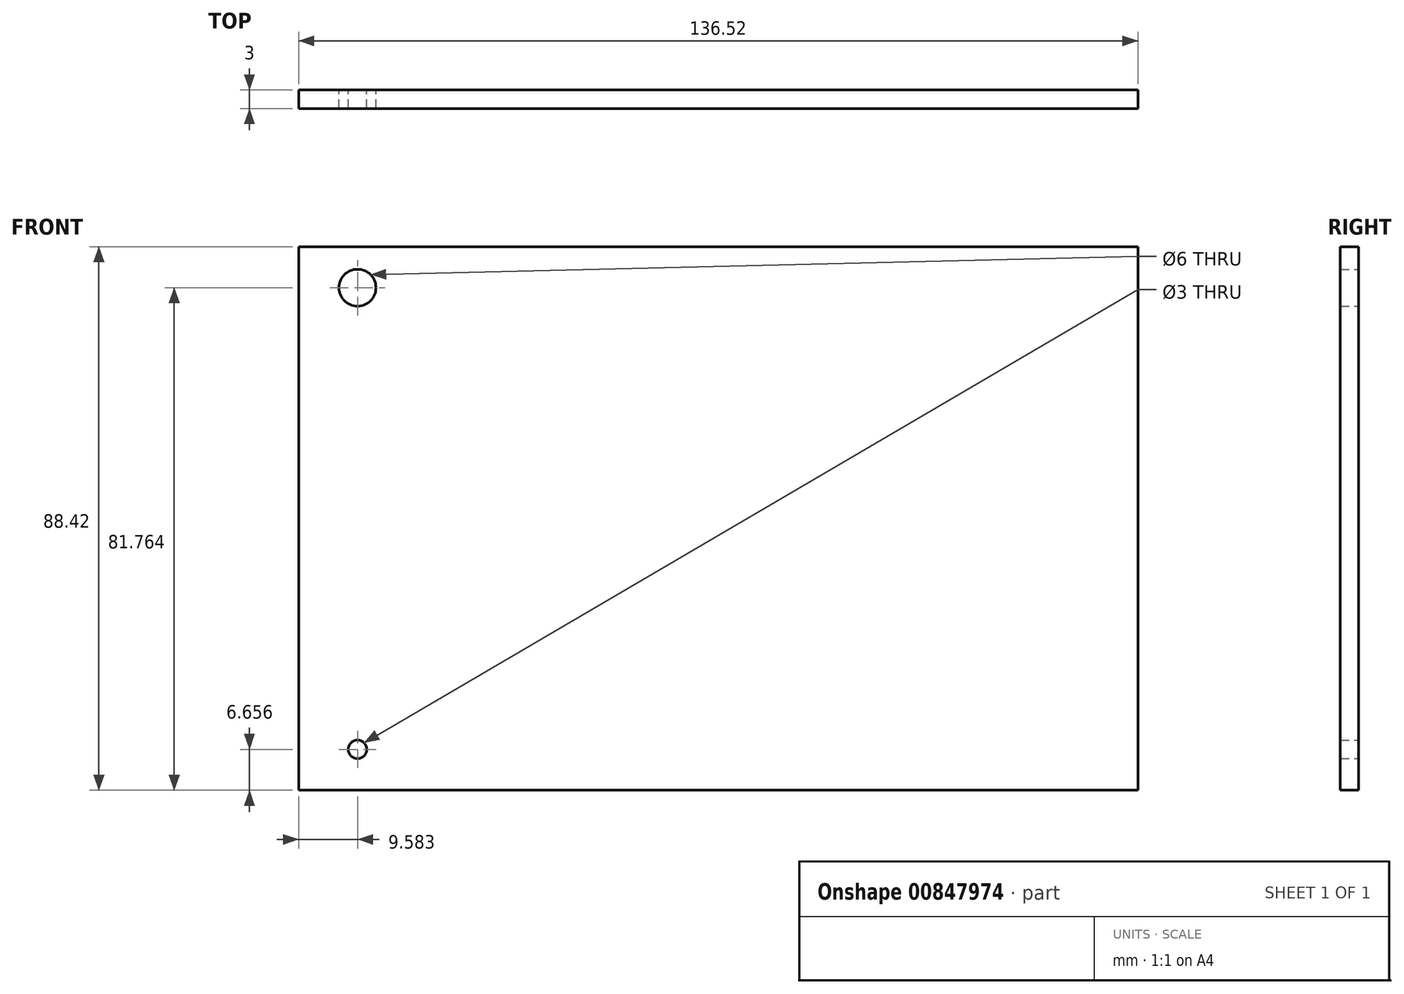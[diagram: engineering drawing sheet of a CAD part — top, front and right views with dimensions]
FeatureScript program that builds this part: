
annotation { "Feature Type Name" : "Feature", "Feature Type Description" : "" }
export const myFeature = defineFeature(function(context is Context, id is Id, definition is map)
    precondition{}
    {
        {
            var Q0;
            Q0=qCreatedBy(makeId("Front.planeOp"),FACE);
            var sketch = newSketch(context, id + "F0", { "sketchPlane" : qUnion([Q0])});
            skLineSegment(sketch, "E0.bottom", {"start": v(68.26, 44.21) * mm, "end": v(-68.26, 44.21) * mm});
            skLineSegment(sketch, "E0.top", {"start": v(68.26, -44.21) * mm, "end": v(-68.26, -44.21) * mm});
            skLineSegment(sketch, "E0.left", {"start": v(68.26, 44.21) * mm, "end": v(68.26, -44.21) * mm});
            skLineSegment(sketch, "E0.right", {"start": v(-68.26, 44.21) * mm, "end": v(-68.26, -44.21) * mm});
            skPoint(sketch, "E0.middle", {"position": v(0, 0) * mm});
            skSolve(sketch);
        }
        {
            var Q0;
            Q0=makeQuery(id+"F0.imprint","IMPRINT",FACE,{"disambiguationData":[TD([[makeQuery(id+"F0.imprint","IMPRINT",EDGE,{"derivedFrom":sQuery(id+"F0.wireOp",EDGE,"E0.bottom")}),1.0]])]});
            extrude(context, id + "F1", {"entities" : qUnion([Q0]), "depth" : 3 * mm, "offsetDistance" : 25.4 * mm});
        }
        {
            var Q0;
            Q0=sQuery(id+"F0.wireOp",VERTEX,"E0.middle");
            var Q1;
            Q1=makeQuery(id+"F1.opExtrude","SWEPT_BODY",BODY,{"disambiguationData":[OSD([sQuery(id+"F0.wireOp",EDGE,"E0.bottom"),sQuery(id+"F0.wireOp",EDGE,"E0.top"),sQuery(id+"F0.wireOp",EDGE,"E0.left"),sQuery(id+"F0.wireOp",EDGE,"E0.right")])]});
            hole(context, id + "F2", {"style" : HoleStyle.SIMPLE, "endStyle" : HoleEndStyle.THROUGH, "oppositeDirection" : true, "holeDiameter" : 30 * mm, "majorDiameter" : 6.35 * mm, "isTappedThrough" : true, "tappedDepth" : 12.7 * mm, "tapClearance" : 3, "locations" : qUnion([Q0]), "scope" : qUnion([Q1])});
        }
        {
            var Q0;
            Q0=qCreatedBy(makeId("Front.planeOp"),FACE);
            var sketch = newSketch(context, id + "F3", { "sketchPlane" : qUnion([Q0])});
            skLineSegment(sketch, "E1.bottom", {"start": v(-58.68, 37.55) * mm, "end": v(58.68, 37.55) * mm});
            skLineSegment(sketch, "E1.top", {"start": v(-58.68, -37.55) * mm, "end": v(58.68, -37.55) * mm});
            skLineSegment(sketch, "E1.left", {"start": v(-58.68, 37.55) * mm, "end": v(-58.68, -37.55) * mm});
            skLineSegment(sketch, "E1.right", {"start": v(58.68, 37.55) * mm, "end": v(58.68, -37.55) * mm});
            skPoint(sketch, "E1.middle", {"position": v(0, 0) * mm});
            skSolve(sketch);
        }
        {
            var Q0;
            Q0 = qSketchRegion(id + "F3", true);
            extrude(context, id + "F4", {"entities" : qUnion([Q0]), "operationType" : NewBodyOperationType.ADD, "depth" : 3 * mm, "offsetDistance" : 25.4 * mm});
        }
        {
            var Q0;
            Q0=sQuery(id+"F3.wireOp",VERTEX,"E1.left.start");
            var Q1;
            Q1=makeQuery(id+"F1.opExtrude","SWEPT_BODY",BODY,{"disambiguationData":[OSD([sQuery(id+"F0.wireOp",EDGE,"E0.bottom"),sQuery(id+"F0.wireOp",EDGE,"E0.top"),sQuery(id+"F0.wireOp",EDGE,"E0.left"),sQuery(id+"F0.wireOp",EDGE,"E0.right")])]});
            hole(context, id + "F5", {"style" : HoleStyle.SIMPLE, "endStyle" : HoleEndStyle.THROUGH, "oppositeDirection" : true, "holeDiameter" : 6 * mm, "majorDiameter" : 6.35 * mm, "isTappedThrough" : true, "tappedDepth" : 12.7 * mm, "tapClearance" : 3, "locations" : qUnion([Q0]), "scope" : qUnion([Q1])});
        }
        {
            var Q0;
            Q0=sQuery(id+"F3.wireOp",VERTEX,"E1.top.start");
            var Q1;
            Q1=sQuery(id+"F3.wireOp",VERTEX,"E1.left.start");
            var Q2;
            Q2=makeQuery(id+"F1.opExtrude","SWEPT_BODY",BODY,{"disambiguationData":[OSD([sQuery(id+"F0.wireOp",EDGE,"E0.bottom"),sQuery(id+"F0.wireOp",EDGE,"E0.top"),sQuery(id+"F0.wireOp",EDGE,"E0.left"),sQuery(id+"F0.wireOp",EDGE,"E0.right")])]});
            hole(context, id + "F6", {"style" : HoleStyle.SIMPLE, "endStyle" : HoleEndStyle.THROUGH, "oppositeDirection" : true, "holeDiameter" : 3 * mm, "majorDiameter" : 6.35 * mm, "isTappedThrough" : true, "tappedDepth" : 12.7 * mm, "tapClearance" : 3, "locations" : qUnion([Q0, Q1]), "scope" : qUnion([Q2])});
        }
    });
